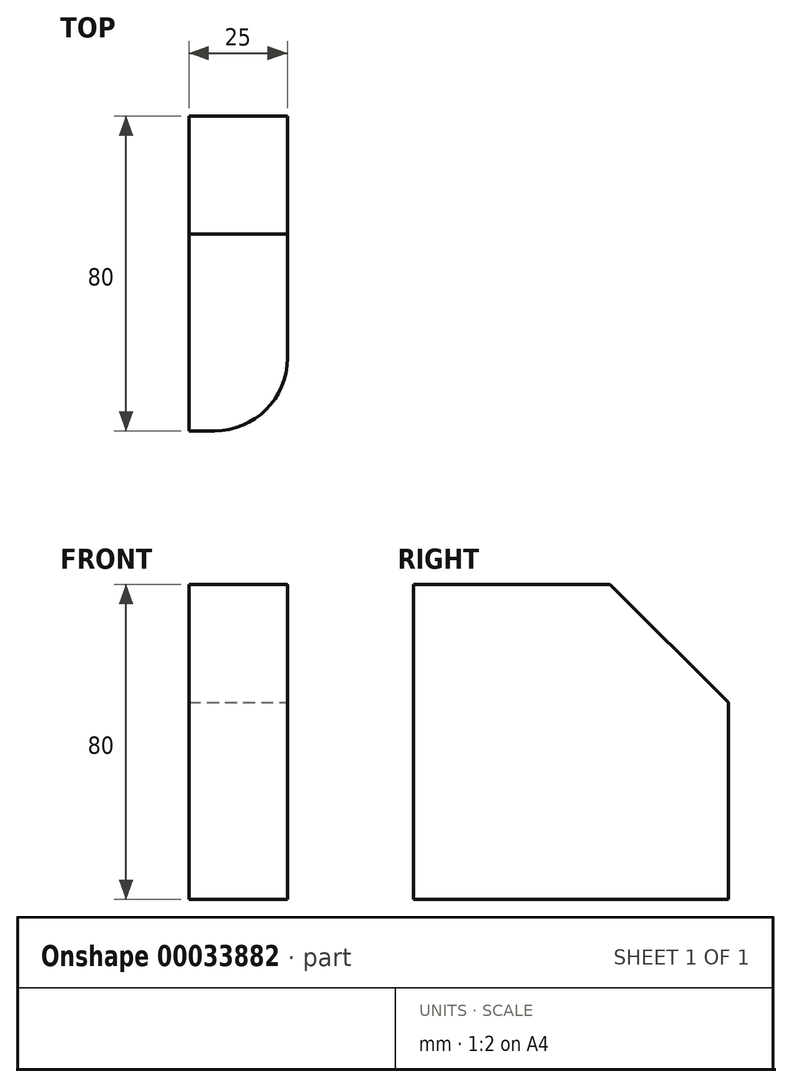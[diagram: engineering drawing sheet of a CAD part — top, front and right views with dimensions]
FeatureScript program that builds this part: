
annotation { "Feature Type Name" : "Feature", "Feature Type Description" : "" }
export const myFeature = defineFeature(function(context is Context, id is Id, definition is map)
    precondition{}
    {
        {
            var Q0;
            Q0=qCreatedBy(makeId("Right.planeOp"),FACE);
            var sketch = newSketch(context, id + "F0", { "sketchPlane" : qUnion([Q0])});
            skLineSegment(sketch, "E0.bottom", {"start": v(-49.42, 66.51) * mm, "end": v(30.58, 66.51) * mm});
            skLineSegment(sketch, "E0.top", {"start": v(-49.42, -13.49) * mm, "end": v(30.58, -13.49) * mm});
            skLineSegment(sketch, "E0.left", {"start": v(-49.42, 66.51) * mm, "end": v(-49.42, -13.49) * mm});
            skLineSegment(sketch, "E0.right", {"start": v(30.58, 66.51) * mm, "end": v(30.58, -13.49) * mm});
            skSolve(sketch);
        }
        {
            var Q0;
            Q0=makeQuery(id+"F0.imprint","IMPRINT",FACE,{"disambiguationData":[TD([[makeQuery(id+"F0.imprint","IMPRINT",EDGE,{"derivedFrom":sQuery(id+"F0.wireOp",EDGE,"E0.bottom")}),-1.0]])]});
            extrude(context, id + "F1", {"entities" : qUnion([Q0]), "depth" : 25 * mm});
        }
        {
            var Q0;
            Q0=makeQuery(id+"F1.opExtrude","SWEPT_EDGE",EDGE,{"disambiguationData":[OSD([sQuery(id+"F0.wireOp",EDGE,"E0.bottom"),sQuery(id+"F0.wireOp",EDGE,"E0.right")])]});
            chamfer(context, id + "F2", {"entities" : qUnion([Q0]), "width" : 30 * mm, "tangentPropagation" : true});
        }
        {
            var Q0;
            Q0=makeQuery(id+"F1.opExtrude","CAP_EDGE",EDGE,{"disambiguationData":[OSD([sQuery(id+"F0.wireOp",EDGE,"E0.left")])],"isStart":false});
            fillet(context, id + "F3", {"entities" : qUnion([Q0]), "radius" : 18.49 * mm, "tangentPropagation" : true, "allowEdgeOverflow" : false});
        }
    });
